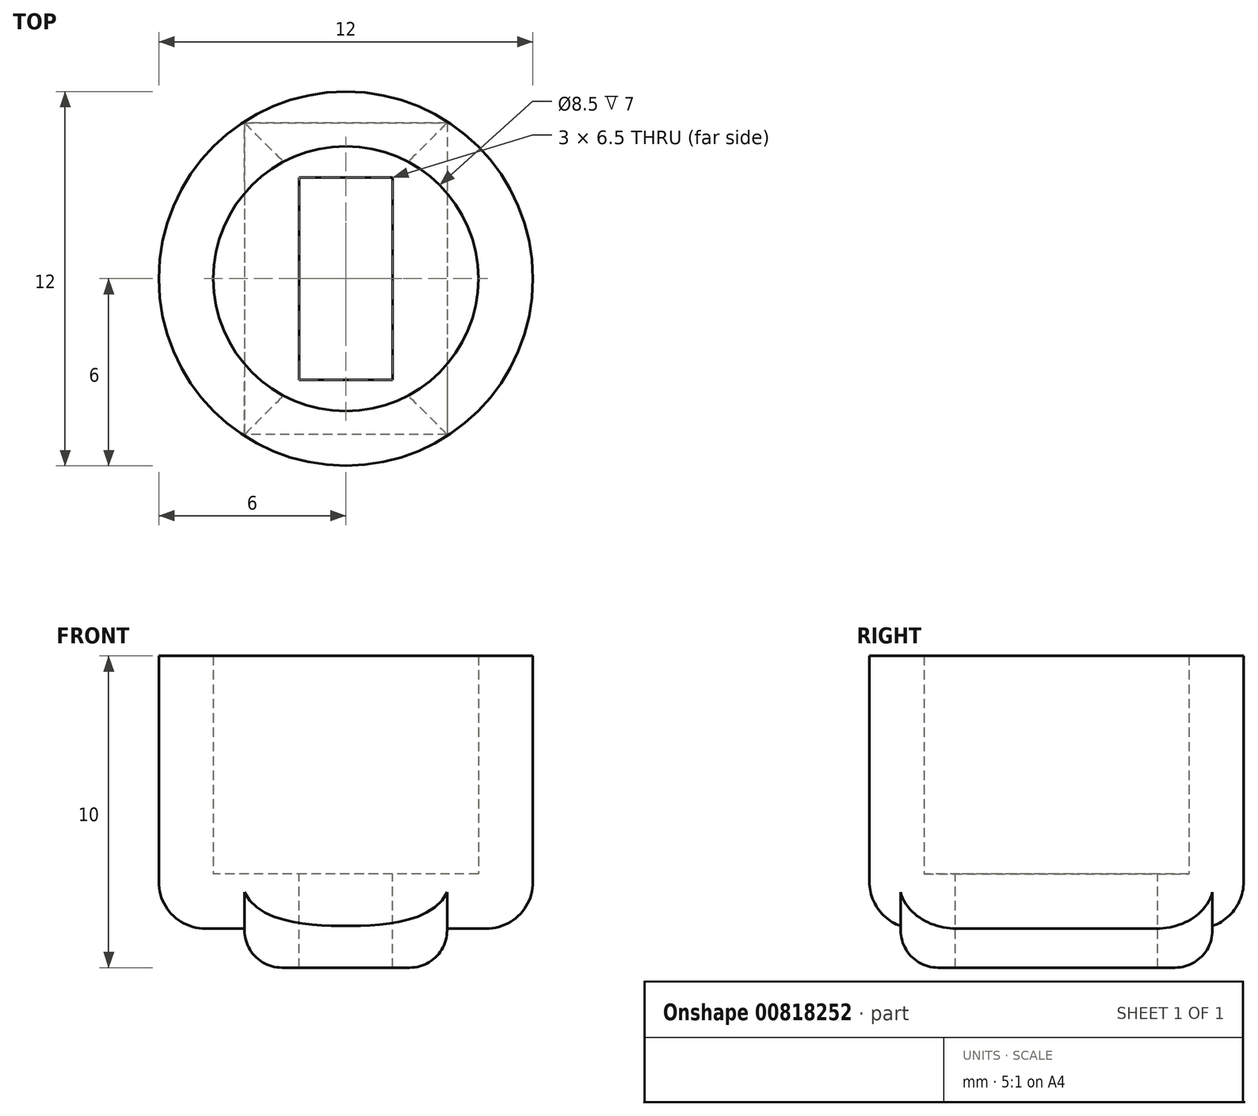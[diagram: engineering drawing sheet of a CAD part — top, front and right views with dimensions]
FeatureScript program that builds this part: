
annotation { "Feature Type Name" : "Feature", "Feature Type Description" : "" }
export const myFeature = defineFeature(function(context is Context, id is Id, definition is map)
    precondition{}
    {
        {
            var Q0;
            Q0=qCreatedBy(makeId("Right.planeOp"),FACE);
            var sketch = newSketch(context, id + "F0", { "sketchPlane" : qUnion([Q0])});
            skLineSegment(sketch, "E0.bottom", {"start": v(3.25, -1.5) * mm, "end": v(-3.25, -1.5) * mm});
            skLineSegment(sketch, "E0.top", {"start": v(3.25, 1.5) * mm, "end": v(-3.25, 1.5) * mm});
            skLineSegment(sketch, "E0.left", {"start": v(3.25, -1.5) * mm, "end": v(3.25, 1.5) * mm});
            skLineSegment(sketch, "E0.right", {"start": v(-3.25, -1.5) * mm, "end": v(-3.25, 1.5) * mm});
            skPoint(sketch, "E0.middle", {"position": v(0, 0) * mm});
            skLineSegment(sketch, "E1.bottom", {"start": v(0, 1.5) * mm, "end": v(-4.25, 1.5) * mm});
            skLineSegment(sketch, "E1.top", {"start": v(0, 8.5) * mm, "end": v(-4.25, 8.5) * mm});
            skLineSegment(sketch, "E1.right", {"start": v(-4.25, 1.5) * mm, "end": v(-4.25, 8.5) * mm});
            skPoint(sketch, "E1.middle", {"position": v(0, 5) * mm});
            skLineSegment(sketch, "E2", {"start": v(0, 13.32) * mm, "end": v(0, -6.18) * mm, "construction": true});
            skPoint(sketch, "E3.orphan", {"position": v(4.25, 1.5) * mm});
            skLineSegment(sketch, "E4", {"start": v(0, 8.5) * mm, "end": v(0, 1.5) * mm});
            skSolve(sketch);
        }
        {
            var Q0;
            Q0=makeQuery(id+"F0.imprint","IMPRINT",FACE,{"disambiguationData":[TD([[makeQuery(id+"F0.imprint","IMPRINT",EDGE,{"derivedFrom":sQuery(id+"F0.wireOp",EDGE,"E0.bottom")}),-1.0]])]});
            extrude(context, id + "F1", {"entities" : qUnion([Q0]), "depth" : 3 * mm, "offsetDistance" : 25 * mm});
        }
        {
            var Q0;
            Q0=makeQuery(id+"F1.opExtrude","SWEPT_FACE",FACE,{"disambiguationData":[OSD([sQuery(id+"F0.wireOp",EDGE,"E0.top"),sQuery(id+"F0.wireOp",EDGE,"E1.bottom")])]});
            var sketch = newSketch(context, id + "F2", { "sketchPlane" : qUnion([Q0])});
            skCircle(sketch, "E5", {"center": v(1.5, 0) * mm, "radius": 4.25 * mm});
            skPoint(sketch, "E5.centerSnap0", {"position": v(1.5, 3.25) * mm});
            skSolve(sketch);
        }
        {
            var Q0;
            Q0 = qSketchRegion(id + "F2", true);
            extrude(context, id + "F3", {"entities" : qUnion([Q0]), "operationType" : NewBodyOperationType.ADD, "depth" : 7 * mm, "offsetDistance" : 25 * mm});
        }
        {
            var Q0;
            Q0=makeQuery(id+"F1.opExtrude","SWEPT_FACE",FACE,{"disambiguationData":[OSD([sQuery(id+"F0.wireOp",EDGE,"E0.bottom")])]});
            var Q1;
            Q1=makeQuery(id+"F3.opExtrude","CAP_FACE",FACE,{"disambiguationData":[OSD([sQuery(id+"F2.wireOp",EDGE,"E5")])],"isStart":false});
            shell(context, id + "F4", {"entities" : qUnion([Q0, Q1]), "thickness" : 1.75 * mm, "oppositeDirection" : true});
        }
        {
            var Q0;
            Q0=makeQuery(id+"F3.opExtrude","CAP_EDGE",EDGE,{"disambiguationData":[OSD([sQuery(id+"F2.wireOp",EDGE,"E5")])],"isStart":true});
            fillet(context, id + "F5", {"entities" : qUnion([Q0]), "radius" : 1.5 * mm, "tangentPropagation" : true, "allowEdgeOverflow" : false});
        }
        {
            var Q0;
            Q0=makeQuery(id+"F1.opExtrude","CAP_EDGE",EDGE,{"disambiguationData":[OSD([sQuery(id+"F0.wireOp",EDGE,"E0.bottom")])],"isStart":false});
            var Q1;
            Q1=makeQuery(id+"F1.opExtrude","SWEPT_EDGE",EDGE,{"disambiguationData":[OSD([sQuery(id+"F0.wireOp",EDGE,"E0.bottom"),sQuery(id+"F0.wireOp",EDGE,"E0.right")])]});
            var Q2;
            Q2=makeQuery(id+"F1.opExtrude","CAP_EDGE",EDGE,{"disambiguationData":[OSD([sQuery(id+"F0.wireOp",EDGE,"E0.bottom")])],"isStart":true});
            var Q3;
            Q3=makeQuery(id+"F1.opExtrude","SWEPT_EDGE",EDGE,{"disambiguationData":[OSD([sQuery(id+"F0.wireOp",EDGE,"E0.bottom"),sQuery(id+"F0.wireOp",EDGE,"E0.left")])]});
            fillet(context, id + "F6", {"entities" : qUnion([Q0, Q1, Q2, Q3]), "radius" : 1.2 * mm, "tangentPropagation" : true, "allowEdgeOverflow" : false});
        }
    });
